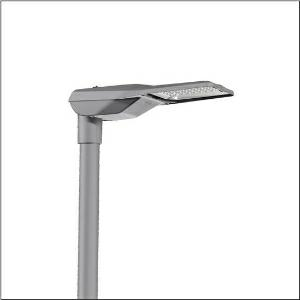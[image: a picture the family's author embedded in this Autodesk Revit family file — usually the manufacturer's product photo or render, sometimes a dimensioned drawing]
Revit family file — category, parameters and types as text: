
# Revit family: streetlight_sl_21_mini___st0_8a_5xe2c43s08gb_a339
name_source: partatom
category: Lighting Fixtures
units: mm (PartAtom-declared; Revit-internal decimal feet)

## family parameters
Cut with Voids When Loaded = No
Host = Face
Light Source = No
Part Type = Normal
Room Calculation Point = No
Round Connector Dimension = Use Diameter
Shared = No

## types (1)
- --- (1 x LED, 6180 lm, 40.4 W, 4000K)
    Apparent Load = 40 VA
    CIE Flux Codes = 38 75 97 100 100
    Color Rendering = 70
    Color Temperature = 4000K
    Default Elevation = 1800 mm
    Description = Streetlight SL 21 mini, mast luminaire, primary light control with lens, of PMMA, primary optical cover: cover, of toughened safety glass, transparent, light distribution: ST0.8a, light emission: direct distribution, primary light characteristic: asymmetric, installation type: side-entry, post-top, LED, High Power LED, rated luminous flux: 6.180lm, luminous efficacy: 153lm/W, light colour: 740, colour temperature: 4000K, control gear: D4i, control: overheat protection, constant luminous flux control, time-dependent luminous flux control, flexible luminous flux parameterisation, pre-setting: logarithmic dimming characteristic, mains connection: 220..240V, AC, 50/60Hz, start of lifetime: 40W, end of service life: 41W, reduction: 19W, luminaire housing, of diecast aluminium, powder-coated, Siteco® metallic grey (DB 702S), corrosivity category C5 mid according to DIN EN ISO 12944, please order mast flange separately, inclination adjustable: 0°, 5°, 10°, 15°, sealing non-destructively replaceable, multi-level sealing system, length: 628mm, width: 235mm, height: 110mm, mast flange for spigot size: 42mm (side-entry): 5XC10008XM4, 60/48mm (side-entry/post-top): 5XC10108XM2, 76/60mm (side-entry/post-top): 5XC10108XM1, mounting height: 4..8m, Smart Interface above, protection rating (complete): IP66, insulation class (complete): insulation class II (safety insulation), certification: CE, ENEC, ENEC+, VDE, impact resistance: IK10, permissible operating ambient temperature for outdoor applications: -40..+50°C, standard-compliant lighting for roads and squares, packaging unit: 1 piece

Light Distribution: ST0.8a
    Height = 110 mm
    Lamp = 1 x LED
    Lamp Light Flux = 6180 lm
    Lamp Power = 40.4 W
    Lamp count = 1
    Length = 625 mm
    Luminous efficacy = 153 lm/W
    Manufacturer = Siteco
    ModVariant = No
    Model = 5XE2C43S08GB
    Number of Poles = 1
    OnlyDefault = Yes
    Power Factor = 1
    Product Name = Streetlight SL 21 mini | ST0.8a
    Product group = mast luminaire | pylon top
    ProductGroupID = 6100
    Protection Class = Protection class II
    Protection Degree = IP 66
    RLX_Detail_Level = 1
    RLX_Emergency_Light_Flux = 0 lm
    RLX_Emergency_Type = 0
    RLX_Emergency_Type_DB = No
    RlxData = <blob elided: 26269 chars, md5=5c6fbb11>
    Socket = socket
    Standby Power = 0 W
    System Light Flux = 6180 lm
    System Power = 40 W
    Type Comments = factory setting: luminous flux: 100 % | dim-lin: 254 | 812 mA
    Type Image = l_1003515.jpg
    URL = http://relux.com
    VarID = @adj_185526
    Voltage = 0 V
    Weight = 0.00 kg
    Width = 234 mm

## geometry (parser evidence)
native form markers: Blend x4, Sweep x11
no freeform markers — native parametric forms only
